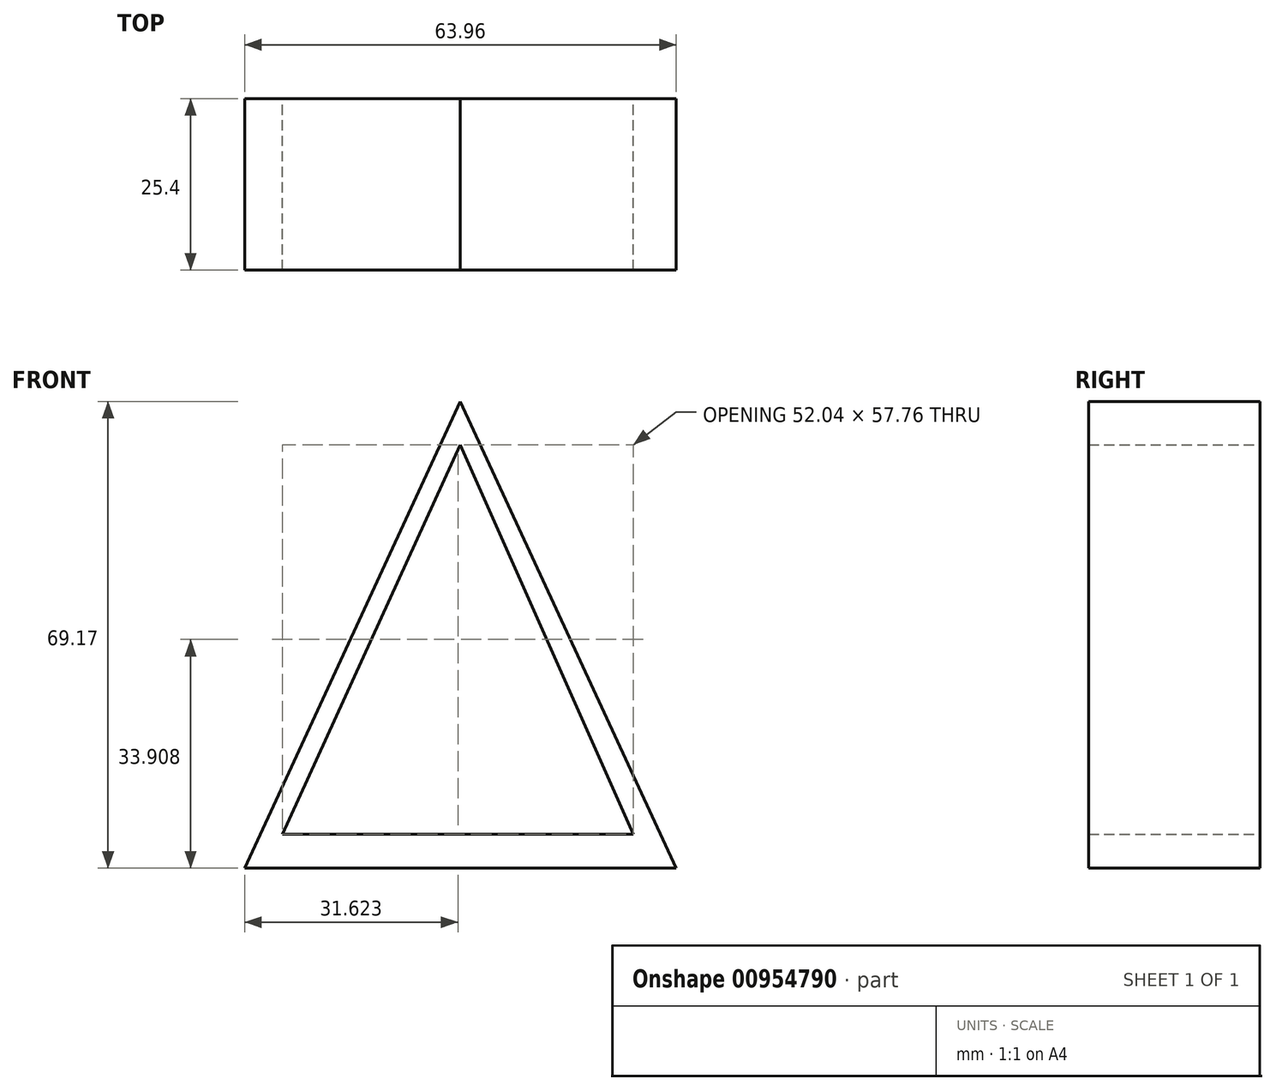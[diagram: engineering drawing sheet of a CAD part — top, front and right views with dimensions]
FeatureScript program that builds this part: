
annotation { "Feature Type Name" : "Feature", "Feature Type Description" : "" }
export const myFeature = defineFeature(function(context is Context, id is Id, definition is map)
    precondition{}
    {
        {
            var Q0;
            Q0=qCreatedBy(makeId("Front.planeOp"),FACE);
            var sketch = newSketch(context, id + "F0", { "sketchPlane" : qUnion([Q0])});
            skLineSegment(sketch, "E0", {"start": v(0, 39.48) * mm, "end": v(-31.98, -29.69) * mm});
            skLineSegment(sketch, "E1", {"start": v(-31.98, -29.69) * mm, "end": v(31.98, -29.69) * mm});
            skLineSegment(sketch, "E2", {"start": v(0, 39.48) * mm, "end": v(31.98, -29.69) * mm});
            skSolve(sketch);
        }
        {
            var Q0;
            Q0 = qSketchRegion(id + "F0", true);
            extrude(context, id + "F1", {"entities" : qUnion([Q0]), "depth" : 25.4 * mm, "offsetDistance" : 25.4 * mm});
        }
        {
            var Q0;
            Q0=qCreatedBy(makeId("Front.planeOp"),FACE);
            var sketch = newSketch(context, id + "F2", { "sketchPlane" : qUnion([Q0])});
            skLineSegment(sketch, "E3", {"start": v(0, 33.1) * mm, "end": v(-26.38, -24.66) * mm});
            skLineSegment(sketch, "E4", {"start": v(-26.38, -24.66) * mm, "end": v(25.66, -24.66) * mm});
            skLineSegment(sketch, "E5", {"start": v(25.66, -24.66) * mm, "end": v(0, 33.1) * mm});
            skSolve(sketch);
        }
        {
            var Q0;
            Q0=makeQuery(id+"F2.imprint","IMPRINT",FACE,{"disambiguationData":[TD([[makeQuery(id+"F2.imprint","IMPRINT",EDGE,{"derivedFrom":sQuery(id+"F2.wireOp",EDGE,"E3")}),1.0]])]});
            extrude(context, id + "F3", {"entities" : qUnion([Q0]), "operationType" : NewBodyOperationType.REMOVE, "depth" : 50.8 * mm, "offsetDistance" : 25.4 * mm});
        }
    });
